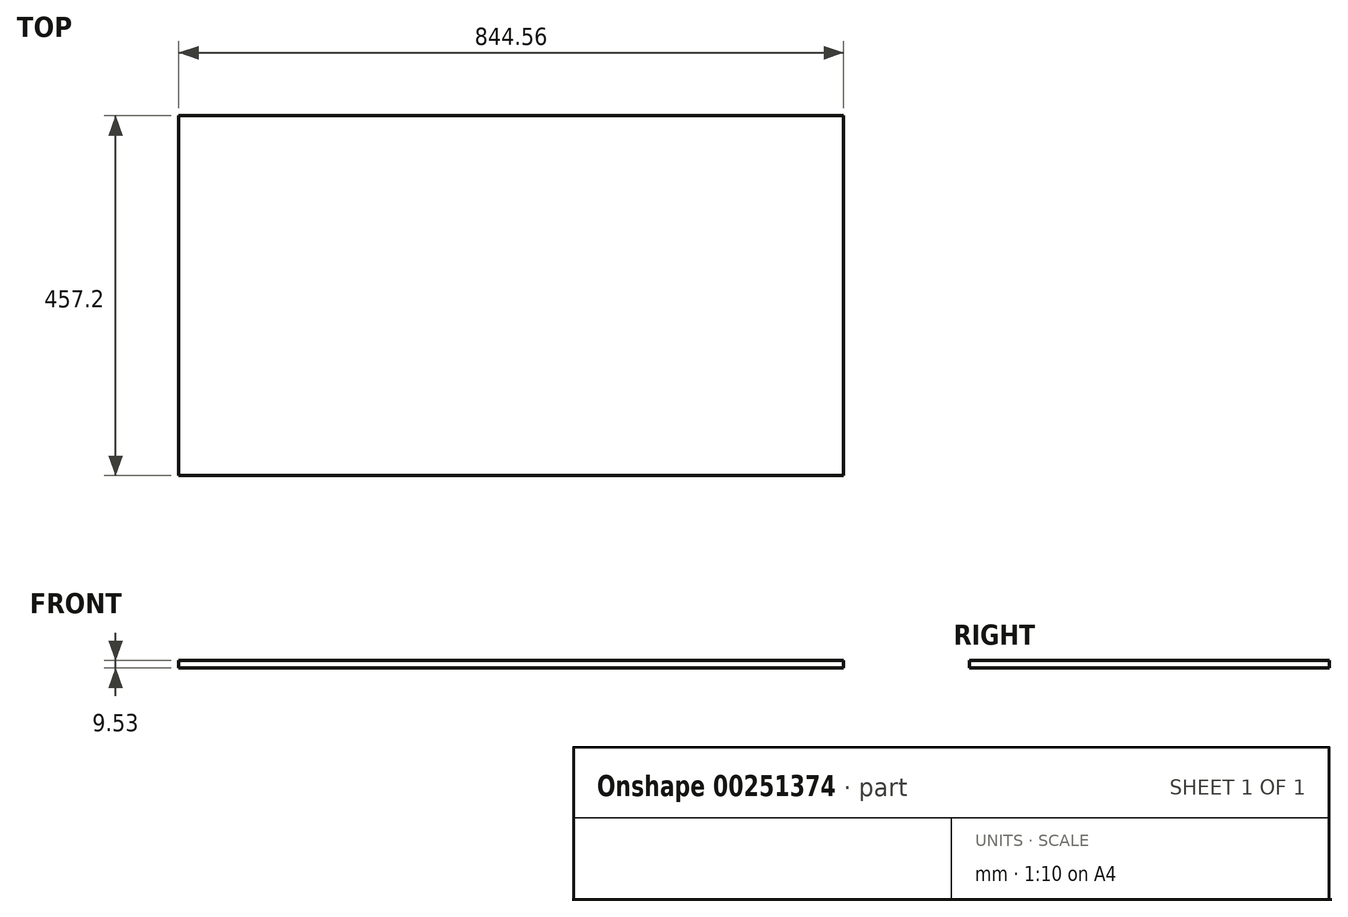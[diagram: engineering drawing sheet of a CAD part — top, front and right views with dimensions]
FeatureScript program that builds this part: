
annotation { "Feature Type Name" : "Feature", "Feature Type Description" : "" }
export const myFeature = defineFeature(function(context is Context, id is Id, definition is map)
    precondition{}
    {
        {
            var Q0;
            Q0=qCreatedBy(makeId("Top.planeOp"),FACE);
            var sketch = newSketch(context, id + "F0", { "sketchPlane" : qUnion([Q0])});
            skLineSegment(sketch, "E0.bottom", {"start": v(-422.28, 228.6) * mm, "end": v(422.28, 228.6) * mm});
            skLineSegment(sketch, "E0.top", {"start": v(-422.28, -228.6) * mm, "end": v(422.28, -228.6) * mm});
            skLineSegment(sketch, "E0.left", {"start": v(-422.28, 228.6) * mm, "end": v(-422.28, -228.6) * mm});
            skLineSegment(sketch, "E0.right", {"start": v(422.28, 228.6) * mm, "end": v(422.28, -228.6) * mm});
            skPoint(sketch, "E0.middle", {"position": v(0, 0) * mm});
            skSolve(sketch);
        }
        {
            var Q0;
            Q0 = qSketchRegion(id + "F0", true);
            extrude(context, id + "F1", {"entities" : qUnion([Q0]), "depth" : 9.52 * mm});
        }
    });
